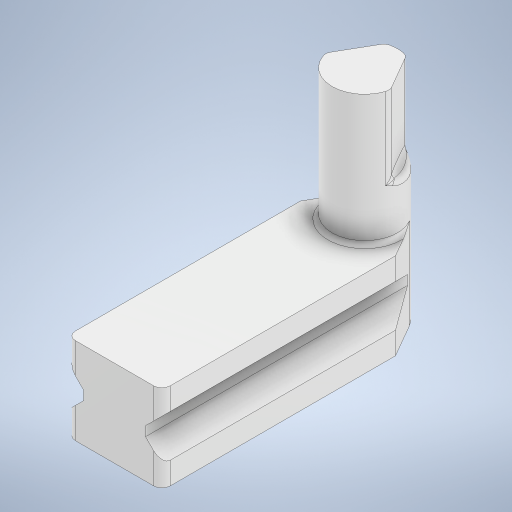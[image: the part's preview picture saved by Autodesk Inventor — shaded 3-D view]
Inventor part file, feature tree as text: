
AUTODESK INVENTOR PART (.ipt)
format: ipt  version: 2024 (Build 280153000, 153)  size: 417,792 bytes
history: native  units: mm
features: fillet x5, extrude x4, sketch x3, projected_geometry x3, chamfer x1, thicken_offset x1
ambient origin geometry x8: Origin, YZ Plane, XZ Plane, XY Plane, X Axis, Y Axis, Z Axis, Center Point
bodies: Solid1 (feature_tree)
feature tree (17):
  extrude  "Extrusion1"  Depth=11.0mm
  chamfer  "Chamfer1"  Distance=35.0mm
  thicken_offset  "Thicken1"
  sketch  "Sketch2"  dims[d2=2.0mm]
  extrude  "Extrusion2"  Depth=2.0mm TaperAngle=45.0deg
  extrude  "Extrusion3"  Depth=1.0mm
  extrude  "Extrusion4"  Depth=1.0mm
  fillet  "Fillet1"  Radius=8.0mm
  fillet  "Fillet2"  [1 undecoded]
  fillet  "Fillet3"  [1 undecoded]
  fillet  "Fillet4"  Radius=16.0mm
  fillet  "Fillet5"  Radius=1.0mm
  sketch  "Sketch1"  dims[d0=8.0mm d1=11.0mm]
  projected_geometry  "Projected Loop1"
  sketch  "Sketch4"  dims[d3=3.0mm d4=35.0mm d5=0.0mm d6=2.0mm d7=2.0mm d8=45.0deg d9=0.2mm d10=0.2mm d11=8.0mm d12=60.0deg d13=0.0mm d14=0.0mm d15=16.0mm d16=0.0mm d17=1.0mm d18=1.0mm d19=10.0mm d20=0.0mm d21=1.0mm d22=0.5mm d23=1.0mm d24=1.0mm d25=1.0mm]
  projected_geometry  "Projected Loop2"
  projected_geometry  "Projected Loop3"
note: 2 required parameter values undecoded (feature->parameter linkage not recoverable at this tier; creation-order binding heuristic only, values carry confidence <= 0.55)
